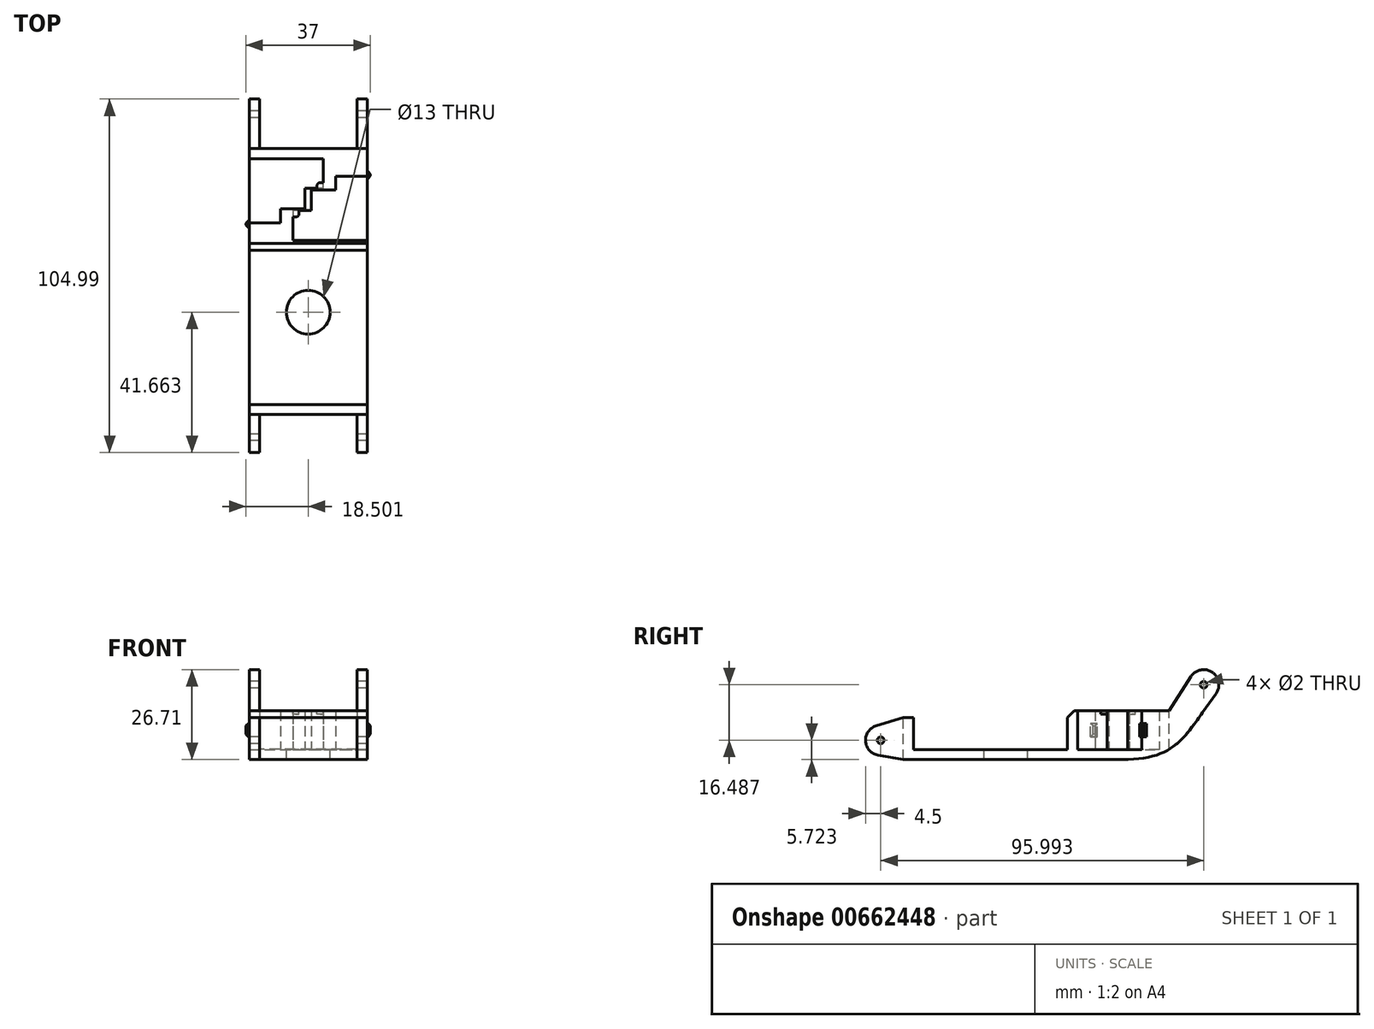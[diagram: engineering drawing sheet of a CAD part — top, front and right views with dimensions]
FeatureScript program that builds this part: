
annotation { "Feature Type Name" : "Feature", "Feature Type Description" : "" }
export const myFeature = defineFeature(function(context is Context, id is Id, definition is map)
    precondition{}
    {
        {
            var Q0;
            Q0=qCreatedBy(makeId("Top.planeOp"),FACE);
            var sketch = newSketch(context, id + "F0", { "sketchPlane" : qUnion([Q0])});
            skLineSegment(sketch, "E0.bottom", {"start": v(-9.64, 16.1) * mm, "end": v(7.86, 16.1) * mm});
            skLineSegment(sketch, "E0.top", {"start": v(-9.64, -29.7) * mm, "end": v(25.36, -29.7) * mm});
            skLineSegment(sketch, "E0.left", {"start": v(-9.64, 16.1) * mm, "end": v(-9.64, -29.7) * mm});
            skLineSegment(sketch, "E1", {"start": v(7.86, 16.1) * mm, "end": v(25.36, 16.1) * mm});
            skCircle(sketch, "E2", {"center": v(7.86, -2.29) * mm, "radius": 6.5 * mm});
            skLineSegment(sketch, "E3.MirrorCS", {"start": v(-9.64, 43.3) * mm, "end": v(-6.47, 43.3) * mm});
            skLineSegment(sketch, "E4.MirrorCS", {"start": v(7.86, 27.9) * mm, "end": v(7.86, 34.5) * mm});
            skLineSegment(sketch, "E5.MirrorCS", {"start": v(-9.64, 24.3) * mm, "end": v(-0.34, 24.3) * mm});
            skLineSegment(sketch, "E6.MirrorCS", {"start": v(12.36, 35.3) * mm, "end": v(12.36, 43.3) * mm});
            skLineSegment(sketch, "E7.MirrorCS", {"start": v(-6.47, 43.3) * mm, "end": v(12.36, 43.3) * mm});
            skLineSegment(sketch, "E8.MirrorCS", {"start": v(-9.64, 24.3) * mm, "end": v(-9.64, 43.3) * mm});
            skPoint(sketch, "E9", {"position": v(7.86, 31.6) * mm});
            skLineSegment(sketch, "E10", {"start": v(-9.64, 16.1) * mm, "end": v(-9.64, 19.1) * mm});
            skLineSegment(sketch, "E11", {"start": v(-9.64, 19.1) * mm, "end": v(25.36, 19.1) * mm});
            skLineSegment(sketch, "E12", {"start": v(-9.64, -29.7) * mm, "end": v(-9.64, -32.7) * mm});
            skLineSegment(sketch, "E13", {"start": v(-9.64, -32.7) * mm, "end": v(25.36, -32.7) * mm});
            skLineSegment(sketch, "E14", {"start": v(25.36, -32.7) * mm, "end": v(25.36, -29.7) * mm});
            skLineSegment(sketch, "E15", {"start": v(25.36, 19.1) * mm, "end": v(25.36, 19.1) * mm});
            skLineSegment(sketch, "E16", {"start": v(25.36, 19.1) * mm, "end": v(25.36, -29.7) * mm});
            skLineSegment(sketch, "E17.MirrorCS", {"start": v(25.36, 19.1) * mm, "end": v(22.2, 19.1) * mm});
            skLineSegment(sketch, "E18.MirrorCS", {"start": v(7.86, 34.5) * mm, "end": v(7.86, 27.9) * mm});
            skLineSegment(sketch, "E19.MirrorCS", {"start": v(25.36, 38.1) * mm, "end": v(16.06, 38.1) * mm});
            skLineSegment(sketch, "E20.MirrorCS", {"start": v(3.36, 27.1) * mm, "end": v(3.36, 19.1) * mm});
            skLineSegment(sketch, "E21.MirrorCS", {"start": v(22.2, 19.1) * mm, "end": v(3.36, 19.1) * mm});
            skLineSegment(sketch, "E22.MirrorCS", {"start": v(25.36, 38.1) * mm, "end": v(25.36, 19.1) * mm});
            skPoint(sketch, "E23", {"position": v(7.86, 30.8) * mm});
            skLineSegment(sketch, "E24", {"start": v(-9.64, 19.1) * mm, "end": v(-9.64, 24.3) * mm});
            skLineSegment(sketch, "E25", {"start": v(12.36, 43.3) * mm, "end": v(25.36, 43.3) * mm});
            skLineSegment(sketch, "E26", {"start": v(25.36, 43.3) * mm, "end": v(25.36, 38.1) * mm});
            skLineSegment(sketch, "E27", {"start": v(-9.64, 43.3) * mm, "end": v(-9.64, 46.3) * mm});
            skLineSegment(sketch, "E28", {"start": v(-9.64, 46.3) * mm, "end": v(25.36, 46.3) * mm});
            skLineSegment(sketch, "E29", {"start": v(25.36, 46.3) * mm, "end": v(25.36, 43.3) * mm});
            skLineSegment(sketch, "E30", {"start": v(25.36, -29.4) * mm, "end": v(-9.64, -29.4) * mm});
            skLineSegment(sketch, "E31", {"start": v(16.06, 38.1) * mm, "end": v(16.06, 34) * mm});
            skLineSegment(sketch, "E32", {"start": v(16.06, 34) * mm, "end": v(7.86, 34) * mm});
            skLineSegment(sketch, "E33", {"start": v(7.86, 34.5) * mm, "end": v(12.36, 34.5) * mm});
            skLineSegment(sketch, "E34", {"start": v(12.36, 34.5) * mm, "end": v(12.36, 35.3) * mm});
            skLineSegment(sketch, "E35", {"start": v(-0.34, 24.3) * mm, "end": v(-0.34, 28.4) * mm});
            skLineSegment(sketch, "E36", {"start": v(7.86, 27.9) * mm, "end": v(3.36, 27.9) * mm});
            skLineSegment(sketch, "E37", {"start": v(3.36, 27.9) * mm, "end": v(3.36, 27.1) * mm});
            skLineSegment(sketch, "E38", {"start": v(7.86, 34.5) * mm, "end": v(6.93, 34.5) * mm});
            skLineSegment(sketch, "E39", {"start": v(7.86, 27.9) * mm, "end": v(8.8, 27.9) * mm});
            skLineSegment(sketch, "E40", {"start": v(6.93, 34.5) * mm, "end": v(6.93, 28.4) * mm});
            skLineSegment(sketch, "E41", {"start": v(8.8, 27.9) * mm, "end": v(8.8, 34) * mm});
            skLineSegment(sketch, "E42", {"start": v(-0.34, 28.4) * mm, "end": v(7.86, 28.4) * mm});
            skSolve(sketch);
        }
        {
            var Q0;
            {var subQ2=sQuery(id+"F0.wireOp",EDGE,"E0.bottom");Q0=makeQuery(id+"F0.imprint","IMPRINT",FACE,{"disambiguationData":[TD([[makeQuery(id+"F0.imprint","IMPRINT",EDGE,{"derivedFrom":subQ2}),-1.0]])]});}
            var Q1;
            Q1=makeQuery(id+"F0.imprint","IMPRINT",FACE,{"disambiguationData":[TD([[makeQuery(id+"F0.imprint","IMPRINT",EDGE,{"derivedFrom":sQuery(id+"F0.wireOp",EDGE,"E0.top")}),-1.0]])]});
            var Q2;
            Q2=makeQuery(id+"F0.imprint","IMPRINT",FACE,{"disambiguationData":[TD([[makeQuery(id+"F0.imprint","IMPRINT",EDGE,{"derivedFrom":sQuery(id+"F0.wireOp",EDGE,"E0.bottom")}),1.0]])]});
            var Q3;
            {var subQ1=sQuery(id+"F0.wireOp",EDGE,"65957815-49e4-4ce0-b1aa-900a07c07509.MirrorCS");Q3=makeQuery(id+"F0.imprint","IMPRINT",FACE,{"disambiguationData":[TD([[makeQuery(id+"F0.imprint","IMPRINT",EDGE,{"derivedFrom":subQ1}),-1.0]])]});}
            var Q4;
            Q4=makeQuery(id+"F0.imprint","IMPRINT",FACE,{"disambiguationData":[TD([[makeQuery(id+"F0.imprint","IMPRINT",EDGE,{"derivedFrom":sQuery(id+"F0.wireOp",EDGE,"793e653a-9070-4513-9301-6aa9de76053a.MirrorCS")}),-1.0]])]});
            var Q5;
            {var subQ3=sQuery(id+"F0.wireOp",EDGE,"bcf4ff58-2fc9-42ac-b040-1ddef6c83d7c.MirrorCS");Q5=makeQuery(id+"F0.imprint","IMPRINT",FACE,{"disambiguationData":[TD([[makeQuery(id+"F0.imprint","IMPRINT",EDGE,{"derivedFrom":subQ3}),1.0]])]});}
            var Q6;
            Q6=makeQuery(id+"F0.imprint","IMPRINT",FACE,{"disambiguationData":[TD([[makeQuery(id+"F0.imprint","IMPRINT",EDGE,{"derivedFrom":sQuery(id+"F0.wireOp",EDGE,"793e653a-9070-4513-9301-6aa9de76053a.MirrorCS")}),1.0]])]});
            var Q7;
            Q7=makeQuery(id+"F0.imprint","IMPRINT",FACE,{"disambiguationData":[TD([[makeQuery(id+"F0.imprint","IMPRINT",EDGE,{"derivedFrom":sQuery(id+"F0.wireOp",EDGE,"E3.MirrorCS")}),1.0]])]});
            var Q8;
            {var subQ0=sQuery(id+"F0.wireOp",EDGE,"E0.top");Q8=makeQuery(id+"F0.imprint","IMPRINT",FACE,{"disambiguationData":[TD([[makeQuery(id+"F0.imprint","IMPRINT",EDGE,{"derivedFrom":subQ0}),1.0]])]});}
            var Q9;
            Q9=makeQuery(id+"F0.imprint","IMPRINT",FACE,{"disambiguationData":[TD([[makeQuery(id+"F0.imprint","IMPRINT",EDGE,{"derivedFrom":sQuery(id+"F0.wireOp",EDGE,"E6.MirrorCS")}),-1.0]])]});
            var Q10;
            Q10=makeQuery(id+"F0.imprint","IMPRINT",FACE,{"disambiguationData":[TD([[makeQuery(id+"F0.imprint","IMPRINT",EDGE,{"derivedFrom":sQuery(id+"F0.wireOp",EDGE,"E5.MirrorCS")}),-1.0]])]});
            var Q11;
            {var subQ3=sQuery(id+"F0.wireOp",EDGE,"E38");Q11=makeQuery(id+"F0.imprint","IMPRINT",FACE,{"disambiguationData":[TD([[makeQuery(id+"F0.imprint","IMPRINT",EDGE,{"derivedFrom":subQ3}),1.0]])]});}
            var Q12;
            {var subQ0=sQuery(id+"F0.wireOp",EDGE,"E39");Q12=makeQuery(id+"F0.imprint","IMPRINT",FACE,{"disambiguationData":[TD([[makeQuery(id+"F0.imprint","IMPRINT",EDGE,{"derivedFrom":subQ0}),1.0]])]});}
            var Q13;
            Q13=makeQuery(id+"F0.imprint","IMPRINT",FACE,{"disambiguationData":[TD([[makeQuery(id+"F0.imprint","IMPRINT",EDGE,{"derivedFrom":sQuery(id+"F0.wireOp",EDGE,"E3.MirrorCS")}),-1.0]])]});
            var Q14;
            Q14=makeQuery(id+"F0.imprint","IMPRINT",FACE,{"disambiguationData":[TD([[makeQuery(id+"F0.imprint","IMPRINT",EDGE,{"derivedFrom":sQuery(id+"F0.wireOp",EDGE,"E19.MirrorCS")}),1.0]])]});
            extrude(context, id + "F1", {"entities" : qUnion([Q0, Q1, Q2, Q3, Q4, Q5, Q6, Q7, Q8, Q9, Q10, Q11, Q12, Q13, Q14]), "oppositeDirection" : true, "depth" : 3 * mm, "offsetDistance" : 25 * mm});
        }
        {
            var Q0;
            Q0=makeQuery(id+"F0.imprint","IMPRINT",FACE,{"disambiguationData":[TD([[makeQuery(id+"F0.imprint","IMPRINT",EDGE,{"derivedFrom":sQuery(id+"F0.wireOp",EDGE,"E0.top")}),-1.0]])]});
            var Q1;
            Q1=makeQuery(id+"F0.imprint","IMPRINT",FACE,{"disambiguationData":[TD([[makeQuery(id+"F0.imprint","IMPRINT",EDGE,{"derivedFrom":sQuery(id+"F0.wireOp",EDGE,"E0.bottom")}),1.0]])]});
            extrude(context, id + "F2", {"entities" : qUnion([Q0, Q1]), "operationType" : NewBodyOperationType.ADD, "depth" : 9.5 * mm, "offsetDistance" : 25 * mm});
        }
        {
            var Q0;
            {var subQ1=sQuery(id+"F0.wireOp",EDGE,"65957815-49e4-4ce0-b1aa-900a07c07509.MirrorCS");Q0=makeQuery(id+"F0.imprint","IMPRINT",FACE,{"disambiguationData":[TD([[makeQuery(id+"F0.imprint","IMPRINT",EDGE,{"derivedFrom":subQ1}),-1.0]])]});}
            var Q1;
            Q1=makeQuery(id+"F0.imprint","IMPRINT",FACE,{"disambiguationData":[TD([[makeQuery(id+"F0.imprint","IMPRINT",EDGE,{"derivedFrom":sQuery(id+"F0.wireOp",EDGE,"793e653a-9070-4513-9301-6aa9de76053a.MirrorCS")}),-1.0]])]});
            var Q2;
            Q2=makeQuery(id+"F0.imprint","IMPRINT",FACE,{"disambiguationData":[TD([[makeQuery(id+"F0.imprint","IMPRINT",EDGE,{"derivedFrom":sQuery(id+"F0.wireOp",EDGE,"E3.MirrorCS")}),1.0]])]});
            var Q3;
            Q3=makeQuery(id+"F0.imprint","IMPRINT",FACE,{"disambiguationData":[TD([[makeQuery(id+"F0.imprint","IMPRINT",EDGE,{"derivedFrom":sQuery(id+"F0.wireOp",EDGE,"E5.MirrorCS")}),-1.0]])]});
            var Q4;
            {var subQ0=sQuery(id+"F0.wireOp",EDGE,"E39");Q4=makeQuery(id+"F0.imprint","IMPRINT",FACE,{"disambiguationData":[TD([[makeQuery(id+"F0.imprint","IMPRINT",EDGE,{"derivedFrom":subQ0}),1.0]])]});}
            var Q5;
            {var subQ3=sQuery(id+"F0.wireOp",EDGE,"E38");Q5=makeQuery(id+"F0.imprint","IMPRINT",FACE,{"disambiguationData":[TD([[makeQuery(id+"F0.imprint","IMPRINT",EDGE,{"derivedFrom":subQ3}),1.0]])]});}
            var Q6;
            Q6=makeQuery(id+"F0.imprint","IMPRINT",FACE,{"disambiguationData":[TD([[makeQuery(id+"F0.imprint","IMPRINT",EDGE,{"derivedFrom":sQuery(id+"F0.wireOp",EDGE,"E6.MirrorCS")}),-1.0]])]});
            var Q7;
            Q7=makeQuery(id+"F0.imprint","IMPRINT",FACE,{"disambiguationData":[TD([[makeQuery(id+"F0.imprint","IMPRINT",EDGE,{"derivedFrom":sQuery(id+"F0.wireOp",EDGE,"E0.bottom")}),1.0]])]});
            extrude(context, id + "F3", {"entities" : qUnion([Q0, Q1, Q2, Q3, Q4, Q5, Q6, Q7]), "operationType" : NewBodyOperationType.ADD, "depth" : 11.5 * mm, "offsetDistance" : 25 * mm});
        }
        {
            var Q0;
            {var subQ0=sQuery(id+"F0.wireOp",EDGE,"E29");var subQ1=sQuery(id+"F0.wireOp",EDGE,"E26");var subQ2=sQuery(id+"F0.wireOp",EDGE,"E16");var subQ3=sQuery(id+"F0.wireOp",EDGE,"E14");Q0=makeQuery(id+"F3.boolean.opBoolean","MERGE",FACE,{"derivedFrom":[makeQuery(id+"F2.boolean.opBoolean","MERGE",FACE,{"derivedFrom":[makeQuery(id+"F1.opExtrude","SWEPT_FACE",FACE,{"disambiguationData":[OSD([subQ3,subQ2,sQuery(id+"F0.wireOp",EDGE,"E22.MirrorCS"),subQ1,subQ0])]}),makeQuery(id+"F2.opExtrude","SWEPT_FACE",FACE,{"disambiguationData":[OSD([subQ3])]}),makeQuery(id+"F2.opExtrude","SWEPT_FACE",FACE,{"disambiguationData":[OSD([subQ2])]})]}),makeQuery(id+"F3.opExtrude","SWEPT_FACE",FACE,{"disambiguationData":[OSD([subQ2])]}),makeQuery(id+"F3.opExtrude","SWEPT_FACE",FACE,{"disambiguationData":[OSD([subQ1,subQ0])]})]});}
            var sketch = newSketch(context, id + "F4", { "sketchPlane" : qUnion([Q0])});
            skLineSegment(sketch, "E43.6", {"start": v(46.3, -3) * mm, "end": v(46.3, 11.5) * mm});
            skLineSegment(sketch, "E43.7", {"start": v(46.3, 11.5) * mm, "end": v(38.1, 11.5) * mm});
            skLineSegment(sketch, "E43.8", {"start": v(-32.7, -3) * mm, "end": v(-32.7, 9.5) * mm});
            skCircle(sketch, "E44", {"center": v(56.54, 19.2) * mm, "radius": 4.5 * mm});
            skLineSegment(sketch, "E45", {"start": v(46.3, -3) * mm, "end": v(60.21, 16.6) * mm});
            skLineSegment(sketch, "E46", {"start": v(46.3, 11.5) * mm, "end": v(52.75, 21.63) * mm});
            skCircle(sketch, "E47", {"center": v(-39.45, 2.72) * mm, "radius": 4.5 * mm});
            skLineSegment(sketch, "E48", {"start": v(-32.7, 9.5) * mm, "end": v(-40.77, 7.03) * mm});
            skLineSegment(sketch, "E49", {"start": v(-32.7, -3) * mm, "end": v(-40.21, -1.71) * mm});
            skSolve(sketch);
        }
        {
            var Q0;
            {var subQ0=sQuery(id+"F4.wireOp",EDGE,"E47");var subQ1=makeQuery(id+"F4.imprint","INTERSECT",VERTEX,{"derivedFrom":[subQ0,sQuery(id+"F4.wireOp",EDGE,"PAik2qhj-YHKu-fe6H-CUS2-yW6YpYjkYPtX")]});Q0=makeQuery(id+"F4.imprint","IMPRINT",FACE,{"disambiguationData":[TD([[makeQuery(id+"F4.imprint","IMPRINT",EDGE,{"disambiguationData":[TD([[subQ1,1.0]])],"derivedFrom":subQ0}),1.0]])]});}
            var Q1;
            Q1=makeQuery(id+"F4.imprint","IMPRINT",FACE,{"disambiguationData":[TD([[makeQuery(id+"F4.imprint","IMPRINT",EDGE,{"derivedFrom":sQuery(id+"F4.wireOp",EDGE,"E43.8")}),1.0]])]});
            var Q2;
            Q2=makeQuery(id+"F4.imprint","IMPRINT",FACE,{"disambiguationData":[TD([[makeQuery(id+"F4.imprint","IMPRINT",EDGE,{"derivedFrom":sQuery(id+"F4.wireOp",EDGE,"E43.6")}),-1.0]])]});
            var Q3;
            {var subQ0=sQuery(id+"F4.wireOp",EDGE,"E44");var subQ1=makeQuery(id+"F4.imprint","INTERSECT",VERTEX,{"derivedFrom":[subQ0,sQuery(id+"F4.wireOp",EDGE,"E45")]});Q3=makeQuery(id+"F4.imprint","IMPRINT",FACE,{"disambiguationData":[TD([[makeQuery(id+"F4.imprint","IMPRINT",EDGE,{"disambiguationData":[TD([[subQ1,1.0]])],"derivedFrom":subQ0}),1.0]])]});}
            extrude(context, id + "F5", {"entities" : qUnion([Q0, Q1, Q2, Q3]), "operationType" : NewBodyOperationType.ADD, "oppositeDirection" : true, "depth" : 3 * mm, "offsetDistance" : 25 * mm});
        }
        {
            var Q0;
            {var subQ0=sQuery(id+"F0.wireOp",EDGE,"E27");var subQ1=sQuery(id+"F0.wireOp",EDGE,"E24");var subQ2=sQuery(id+"F0.wireOp",EDGE,"E10");var subQ3=sQuery(id+"F0.wireOp",EDGE,"E12");Q0=makeQuery(id+"F3.boolean.opBoolean","MERGE",FACE,{"derivedFrom":[makeQuery(id+"F2.boolean.opBoolean","MERGE",FACE,{"derivedFrom":[makeQuery(id+"F1.opExtrude","SWEPT_FACE",FACE,{"disambiguationData":[OSD([sQuery(id+"F0.wireOp",EDGE,"E0.left"),sQuery(id+"F0.wireOp",EDGE,"E8.MirrorCS"),subQ2,subQ3,subQ1,subQ0])]}),makeQuery(id+"F2.opExtrude","SWEPT_FACE",FACE,{"disambiguationData":[OSD([subQ2])]}),makeQuery(id+"F2.opExtrude","SWEPT_FACE",FACE,{"disambiguationData":[OSD([subQ3])]})]}),makeQuery(id+"F3.opExtrude","SWEPT_FACE",FACE,{"disambiguationData":[OSD([subQ2,subQ1])]}),makeQuery(id+"F3.opExtrude","SWEPT_FACE",FACE,{"disambiguationData":[OSD([subQ0])]})]});}
            var sketch = newSketch(context, id + "F6", { "sketchPlane" : qUnion([Q0])});
            skLineSegment(sketch, "E50.0", {"start": v(-46.3, -3) * mm, "end": v(-60.21, 16.6) * mm});
            skArc(sketch, "E50.1", {"start": v(-60.21, 16.6) * mm, "mid": v(-59.06, 22.94) * mm, "end": v(-52.75, 21.63) * mm});
            skLineSegment(sketch, "E50.2", {"start": v(-46.3, 11.5) * mm, "end": v(-52.75, 21.63) * mm});
            skLineSegment(sketch, "E50.3", {"start": v(-46.3, -3) * mm, "end": v(-46.3, 11.5) * mm});
            skLineSegment(sketch, "E50.4", {"start": v(32.7, -3) * mm, "end": v(32.7, 9.5) * mm});
            skLineSegment(sketch, "E50.5", {"start": v(32.7, 9.5) * mm, "end": v(40.77, 7.03) * mm});
            skArc(sketch, "E50.6", {"start": v(40.77, 7.03) * mm, "mid": v(43.94, 2.44) * mm, "end": v(40.21, -1.71) * mm});
            skLineSegment(sketch, "E50.7", {"start": v(32.7, -3) * mm, "end": v(40.21, -1.71) * mm});
            skSolve(sketch);
        }
        {
            var Q0;
            Q0=makeQuery(id+"F6.imprint","IMPRINT",FACE,{"disambiguationData":[TD([[makeQuery(id+"F6.imprint","IMPRINT",EDGE,{"derivedFrom":sQuery(id+"F6.wireOp",EDGE,"E50.0")}),-1.0]])]});
            var Q1;
            Q1=makeQuery(id+"F6.imprint","IMPRINT",FACE,{"disambiguationData":[TD([[makeQuery(id+"F6.imprint","IMPRINT",EDGE,{"derivedFrom":sQuery(id+"F6.wireOp",EDGE,"E50.4")}),-1.0]])]});
            extrude(context, id + "F7", {"entities" : qUnion([Q0, Q1]), "operationType" : NewBodyOperationType.ADD, "oppositeDirection" : true, "depth" : 3 * mm, "offsetDistance" : 25 * mm});
        }
        {
            var Q0;
            {var subQ0=sQuery(id+"F0.wireOp",EDGE,"E27");var subQ1=sQuery(id+"F0.wireOp",EDGE,"E24");var subQ2=sQuery(id+"F0.wireOp",EDGE,"E10");var subQ3=sQuery(id+"F0.wireOp",EDGE,"E12");Q0=makeQuery(id+"F7.boolean.opBoolean","MERGE",FACE,{"derivedFrom":[makeQuery(id+"F3.boolean.opBoolean","MERGE",FACE,{"derivedFrom":[makeQuery(id+"F2.boolean.opBoolean","MERGE",FACE,{"derivedFrom":[makeQuery(id+"F1.opExtrude","SWEPT_FACE",FACE,{"disambiguationData":[OSD([sQuery(id+"F0.wireOp",EDGE,"E0.left"),sQuery(id+"F0.wireOp",EDGE,"E8.MirrorCS"),subQ2,subQ3,subQ1,subQ0])]}),makeQuery(id+"F2.opExtrude","SWEPT_FACE",FACE,{"disambiguationData":[OSD([subQ2])]}),makeQuery(id+"F2.opExtrude","SWEPT_FACE",FACE,{"disambiguationData":[OSD([subQ3])]})]}),makeQuery(id+"F3.opExtrude","SWEPT_FACE",FACE,{"disambiguationData":[OSD([subQ2,subQ1])]}),makeQuery(id+"F3.opExtrude","SWEPT_FACE",FACE,{"disambiguationData":[OSD([subQ0])]})]}),makeQuery(id+"F7.opExtrude","CAP_FACE",FACE,{"disambiguationData":[OSD([sQuery(id+"F6.wireOp",EDGE,"E50.0"),sQuery(id+"F6.wireOp",EDGE,"E50.1"),sQuery(id+"F6.wireOp",EDGE,"E50.2"),sQuery(id+"F6.wireOp",EDGE,"E50.3")])],"isStart":true}),makeQuery(id+"F7.opExtrude","CAP_FACE",FACE,{"disambiguationData":[OSD([sQuery(id+"F6.wireOp",EDGE,"E50.4"),sQuery(id+"F6.wireOp",EDGE,"E50.5"),sQuery(id+"F6.wireOp",EDGE,"E50.6"),sQuery(id+"F6.wireOp",EDGE,"E50.7")])],"isStart":true})]});}
            var sketch = newSketch(context, id + "F8", { "sketchPlane" : qUnion([Q0])});
            skArc(sketch, "E51.0", {"start": v(-60.21, 16.6) * mm, "mid": v(-59.06, 22.94) * mm, "end": v(-52.75, 21.63) * mm});
            skArc(sketch, "E51.1", {"start": v(40.77, 7.03) * mm, "mid": v(43.94, 2.44) * mm, "end": v(40.21, -1.71) * mm});
            skCircle(sketch, "E52", {"center": v(-56.54, 19.2) * mm, "radius": 1 * mm});
            skCircle(sketch, "E53", {"center": v(39.45, 2.72) * mm, "radius": 1 * mm});
            skSolve(sketch);
        }
        {
            var Q0;
            Q0=makeQuery(id+"F8.imprint","IMPRINT",FACE,{"disambiguationData":[TD([[makeQuery(id+"F8.imprint","IMPRINT",EDGE,{"derivedFrom":sQuery(id+"F8.wireOp",EDGE,"E52")}),1.0]])]});
            var Q1;
            Q1=makeQuery(id+"F8.imprint","IMPRINT",FACE,{"disambiguationData":[TD([[makeQuery(id+"F8.imprint","IMPRINT",EDGE,{"derivedFrom":sQuery(id+"F8.wireOp",EDGE,"E53")}),1.0]])]});
            extrude(context, id + "F9", {"entities" : qUnion([Q0, Q1]), "operationType" : NewBodyOperationType.REMOVE, "endBound" : BoundingType.THROUGH_ALL, "oppositeDirection" : true, "depth" : 25 * mm, "offsetDistance" : 25 * mm});
        }
        {
            var Q0;
            {var subQ0=sQuery(id+"F0.wireOp",EDGE,"E29");var subQ1=sQuery(id+"F0.wireOp",EDGE,"E26");var subQ2=sQuery(id+"F0.wireOp",EDGE,"E16");var subQ3=sQuery(id+"F0.wireOp",EDGE,"E14");Q0=makeQuery(id+"F5.boolean.opBoolean","MERGE",FACE,{"derivedFrom":[makeQuery(id+"F3.boolean.opBoolean","MERGE",FACE,{"derivedFrom":[makeQuery(id+"F2.boolean.opBoolean","MERGE",FACE,{"derivedFrom":[makeQuery(id+"F1.opExtrude","SWEPT_FACE",FACE,{"disambiguationData":[OSD([subQ3,subQ2,sQuery(id+"F0.wireOp",EDGE,"E22.MirrorCS"),subQ1,subQ0])]}),makeQuery(id+"F2.opExtrude","SWEPT_FACE",FACE,{"disambiguationData":[OSD([subQ3])]}),makeQuery(id+"F2.opExtrude","SWEPT_FACE",FACE,{"disambiguationData":[OSD([subQ2])]})]}),makeQuery(id+"F3.opExtrude","SWEPT_FACE",FACE,{"disambiguationData":[OSD([subQ2])]}),makeQuery(id+"F3.opExtrude","SWEPT_FACE",FACE,{"disambiguationData":[OSD([subQ1,subQ0])]})]}),makeQuery(id+"F5.opExtrude","CAP_FACE",FACE,{"disambiguationData":[OSD([sQuery(id+"F4.wireOp",EDGE,"E43.6"),sQuery(id+"F4.wireOp",EDGE,"E44"),sQuery(id+"F4.wireOp",EDGE,"E45"),sQuery(id+"F4.wireOp",EDGE,"E46")])],"isStart":true}),makeQuery(id+"F5.opExtrude","CAP_FACE",FACE,{"disambiguationData":[OSD([sQuery(id+"F4.wireOp",EDGE,"E43.8"),sQuery(id+"F4.wireOp",EDGE,"E47"),sQuery(id+"F4.wireOp",EDGE,"E48"),sQuery(id+"F4.wireOp",EDGE,"E49")])],"isStart":true})]});}
            var sketch = newSketch(context, id + "F10", { "sketchPlane" : qUnion([Q0])});
            skLineSegment(sketch, "E54.0", {"start": v(38.1, 11.5) * mm, "end": v(38.1, 0) * mm});
            skPoint(sketch, "E55", {"position": v(38.1, 5.75) * mm});
            skLineSegment(sketch, "E56", {"start": v(35.03, 5.75) * mm, "end": v(42.1, 5.75) * mm, "construction": true});
            skLineSegment(sketch, "E57", {"start": v(37.5, 5.75) * mm, "end": v(37.5, 7.75) * mm});
            skLineSegment(sketch, "E58", {"start": v(37.5, 7.75) * mm, "end": v(39.5, 7.75) * mm});
            skLineSegment(sketch, "E59", {"start": v(39.5, 7.75) * mm, "end": v(39.5, 5.75) * mm});
            skLineSegment(sketch, "E60.MirrorCS", {"start": v(37.5, 3.75) * mm, "end": v(39.5, 3.75) * mm});
            skLineSegment(sketch, "E61.MirrorCS", {"start": v(37.5, 5.75) * mm, "end": v(37.5, 3.75) * mm});
            skLineSegment(sketch, "E62.MirrorCS", {"start": v(39.5, 3.75) * mm, "end": v(39.5, 5.75) * mm});
            skSolve(sketch);
        }
        {
            var Q0;
            {var subQ4=sQuery(id+"F10.wireOp",EDGE,"E59");Q0=makeQuery(id+"F10.imprint","IMPRINT",FACE,{"disambiguationData":[TD([[makeQuery(id+"F10.imprint","IMPRINT",EDGE,{"derivedFrom":subQ4}),-1.0]])]});}
            var Q1;
            {var subQ5=sQuery(id+"F10.wireOp",EDGE,"E57");Q1=makeQuery(id+"F10.imprint","IMPRINT",FACE,{"disambiguationData":[TD([[makeQuery(id+"F10.imprint","IMPRINT",EDGE,{"derivedFrom":subQ5}),-1.0]])]});}
            extrude(context, id + "F11", {"entities" : qUnion([Q0, Q1]), "operationType" : NewBodyOperationType.ADD, "depth" : 1 * mm, "offsetDistance" : 25 * mm});
        }
        {
            var Q0;
            {var subQ0=sQuery(id+"F0.wireOp",EDGE,"E27");var subQ1=sQuery(id+"F0.wireOp",EDGE,"E24");var subQ2=sQuery(id+"F0.wireOp",EDGE,"E10");var subQ3=sQuery(id+"F0.wireOp",EDGE,"E12");Q0=makeQuery(id+"F7.boolean.opBoolean","MERGE",FACE,{"derivedFrom":[makeQuery(id+"F3.boolean.opBoolean","MERGE",FACE,{"derivedFrom":[makeQuery(id+"F2.boolean.opBoolean","MERGE",FACE,{"derivedFrom":[makeQuery(id+"F1.opExtrude","SWEPT_FACE",FACE,{"disambiguationData":[OSD([sQuery(id+"F0.wireOp",EDGE,"E0.left"),sQuery(id+"F0.wireOp",EDGE,"E8.MirrorCS"),subQ2,subQ3,subQ1,subQ0])]}),makeQuery(id+"F2.opExtrude","SWEPT_FACE",FACE,{"disambiguationData":[OSD([subQ2])]}),makeQuery(id+"F2.opExtrude","SWEPT_FACE",FACE,{"disambiguationData":[OSD([subQ3])]})]}),makeQuery(id+"F3.opExtrude","SWEPT_FACE",FACE,{"disambiguationData":[OSD([subQ2,subQ1])]}),makeQuery(id+"F3.opExtrude","SWEPT_FACE",FACE,{"disambiguationData":[OSD([subQ0])]})]}),makeQuery(id+"F7.opExtrude","CAP_FACE",FACE,{"disambiguationData":[OSD([sQuery(id+"F6.wireOp",EDGE,"E50.0"),sQuery(id+"F6.wireOp",EDGE,"E50.1"),sQuery(id+"F6.wireOp",EDGE,"E50.2"),sQuery(id+"F6.wireOp",EDGE,"E50.3")])],"isStart":true}),makeQuery(id+"F7.opExtrude","CAP_FACE",FACE,{"disambiguationData":[OSD([sQuery(id+"F6.wireOp",EDGE,"E50.4"),sQuery(id+"F6.wireOp",EDGE,"E50.5"),sQuery(id+"F6.wireOp",EDGE,"E50.6"),sQuery(id+"F6.wireOp",EDGE,"E50.7")])],"isStart":true})]});}
            var sketch = newSketch(context, id + "F12", { "sketchPlane" : qUnion([Q0])});
            skLineSegment(sketch, "E63", {"start": v(-24.3, 5.75) * mm, "end": v(-30.81, 5.75) * mm, "construction": true});
            skLineSegment(sketch, "E64", {"start": v(-24.9, 5.75) * mm, "end": v(-24.9, 7.75) * mm});
            skLineSegment(sketch, "E65", {"start": v(-24.9, 7.75) * mm, "end": v(-22.9, 7.75) * mm});
            skLineSegment(sketch, "E66", {"start": v(-22.9, 7.75) * mm, "end": v(-22.9, 5.75) * mm});
            skLineSegment(sketch, "E67.MirrorCS", {"start": v(-24.9, 5.75) * mm, "end": v(-24.9, 3.75) * mm});
            skLineSegment(sketch, "E68.MirrorCS", {"start": v(-22.9, 3.75) * mm, "end": v(-22.9, 5.75) * mm});
            skLineSegment(sketch, "E69.MirrorCS", {"start": v(-24.9, 3.75) * mm, "end": v(-22.9, 3.75) * mm});
            skSolve(sketch);
        }
        {
            var Q0;
            {var subQ1=sQuery(id+"F12.wireOp",EDGE,"E66");Q0=makeQuery(id+"F12.imprint","IMPRINT",FACE,{"disambiguationData":[TD([[makeQuery(id+"F12.imprint","IMPRINT",EDGE,{"derivedFrom":subQ1}),-1.0]])]});}
            var Q1;
            {var subQ5=sQuery(id+"F12.wireOp",EDGE,"E64");Q1=makeQuery(id+"F12.imprint","IMPRINT",FACE,{"disambiguationData":[TD([[makeQuery(id+"F12.imprint","IMPRINT",EDGE,{"derivedFrom":subQ5}),-1.0]])]});}
            extrude(context, id + "F13", {"entities" : qUnion([Q0, Q1]), "operationType" : NewBodyOperationType.ADD, "depth" : 1 * mm, "offsetDistance" : 25 * mm});
        }
        {
            var Q0;
            Q0=makeQuery(id+"F13.opExtrude","CAP_EDGE",EDGE,{"disambiguationData":[OSD([sQuery(id+"F12.wireOp",EDGE,"E64"),sQuery(id+"F12.wireOp",EDGE,"E67.MirrorCS")])],"isStart":false});
            var Q1;
            Q1=makeQuery(id+"F13.opExtrude","CAP_EDGE",EDGE,{"disambiguationData":[OSD([sQuery(id+"F12.wireOp",EDGE,"E66"),sQuery(id+"F12.wireOp",EDGE,"E68.MirrorCS")])],"isStart":false});
            var Q2;
            Q2=makeQuery(id+"F13.opExtrude","CAP_EDGE",EDGE,{"disambiguationData":[OSD([sQuery(id+"F12.wireOp",EDGE,"E65")])],"isStart":false});
            var Q3;
            Q3=makeQuery(id+"F13.opExtrude","CAP_EDGE",EDGE,{"disambiguationData":[OSD([sQuery(id+"F12.wireOp",EDGE,"E69.MirrorCS")])],"isStart":false});
            var Q4;
            Q4=makeQuery(id+"F11.opExtrude","CAP_EDGE",EDGE,{"disambiguationData":[OSD([sQuery(id+"F10.wireOp",EDGE,"E58")])],"isStart":false});
            var Q5;
            Q5=makeQuery(id+"F11.opExtrude","CAP_EDGE",EDGE,{"disambiguationData":[OSD([sQuery(id+"F10.wireOp",EDGE,"E57"),sQuery(id+"F10.wireOp",EDGE,"E61.MirrorCS")])],"isStart":false});
            var Q6;
            Q6=makeQuery(id+"F11.opExtrude","CAP_EDGE",EDGE,{"disambiguationData":[OSD([sQuery(id+"F10.wireOp",EDGE,"E60.MirrorCS")])],"isStart":false});
            var Q7;
            Q7=makeQuery(id+"F11.opExtrude","CAP_EDGE",EDGE,{"disambiguationData":[OSD([sQuery(id+"F10.wireOp",EDGE,"E59"),sQuery(id+"F10.wireOp",EDGE,"E62.MirrorCS")])],"isStart":false});
            chamfer(context, id + "F14", {"entities" : qUnion([Q0, Q1, Q2, Q3, Q4, Q5, Q6, Q7]), "width" : .75 * mm, "tangentPropagation" : true});
        }
        {
            var Q0;
            Q0=makeQuery(id+"F3.opExtrude","CAP_FACE",FACE,{"disambiguationData":[OSD([sQuery(id+"F0.wireOp",EDGE,"E0.bottom"),sQuery(id+"F0.wireOp",EDGE,"E1"),sQuery(id+"F0.wireOp",EDGE,"E3.MirrorCS"),sQuery(id+"F0.wireOp",EDGE,"E5.MirrorCS"),sQuery(id+"F0.wireOp",EDGE,"E6.MirrorCS"),sQuery(id+"F0.wireOp",EDGE,"E7.MirrorCS"),sQuery(id+"F0.wireOp",EDGE,"E10"),sQuery(id+"F0.wireOp",EDGE,"E11"),sQuery(id+"F0.wireOp",EDGE,"E16"),sQuery(id+"F0.wireOp",EDGE,"E19.MirrorCS"),sQuery(id+"F0.wireOp",EDGE,"E20.MirrorCS"),sQuery(id+"F0.wireOp",EDGE,"E24"),sQuery(id+"F0.wireOp",EDGE,"E26"),sQuery(id+"F0.wireOp",EDGE,"E27"),sQuery(id+"F0.wireOp",EDGE,"E28"),sQuery(id+"F0.wireOp",EDGE,"E29"),sQuery(id+"F0.wireOp",EDGE,"E31"),sQuery(id+"F0.wireOp",EDGE,"E32"),sQuery(id+"F0.wireOp",EDGE,"E33"),sQuery(id+"F0.wireOp",EDGE,"E34"),sQuery(id+"F0.wireOp",EDGE,"E35"),sQuery(id+"F0.wireOp",EDGE,"E36"),sQuery(id+"F0.wireOp",EDGE,"E37"),sQuery(id+"F0.wireOp",EDGE,"E38"),sQuery(id+"F0.wireOp",EDGE,"E39"),sQuery(id+"F0.wireOp",EDGE,"E40"),sQuery(id+"F0.wireOp",EDGE,"E41"),sQuery(id+"F0.wireOp",EDGE,"E42")])],"isStart":false});
            var sketch = newSketch(context, id + "F15", { "sketchPlane" : qUnion([Q0])});
            skLineSegment(sketch, "E70.0", {"start": v(12.36, 34.5) * mm, "end": v(6.93, 34.5) * mm});
            skLineSegment(sketch, "E70.1", {"start": v(8.8, 27.9) * mm, "end": v(3.36, 27.9) * mm});
            skLineSegment(sketch, "E71", {"start": v(5.12, 27.9) * mm, "end": v(5.12, 25.96) * mm});
            skPoint(sketch, "E71.endSnap0", {"position": v(3.36, 25.96) * mm});
            skLineSegment(sketch, "E72", {"start": v(5.12, 25.96) * mm, "end": v(3.36, 25.96) * mm});
            skLineSegment(sketch, "E73", {"start": v(3.36, 27.9) * mm, "end": v(3.36, 25.96) * mm});
            skLineSegment(sketch, "E74", {"start": v(10.48, 34.5) * mm, "end": v(10.48, 36.23) * mm});
            skPoint(sketch, "E74.endSnap0", {"position": v(12.36, 36.23) * mm});
            skLineSegment(sketch, "E75", {"start": v(10.48, 36.23) * mm, "end": v(12.36, 36.23) * mm});
            skSolve(sketch);
        }
        {
            var Q0;
            {var subQ3=sQuery(id+"F15.wireOp",EDGE,"E74");Q0=makeQuery(id+"F15.imprint","IMPRINT",FACE,{"disambiguationData":[TD([[makeQuery(id+"F15.imprint","IMPRINT",EDGE,{"derivedFrom":subQ3}),-1.0]])]});}
            var Q1;
            {var subQ2=sQuery(id+"F15.wireOp",EDGE,"E71");Q1=makeQuery(id+"F15.imprint","IMPRINT",FACE,{"disambiguationData":[TD([[makeQuery(id+"F15.imprint","IMPRINT",EDGE,{"derivedFrom":subQ2}),-1.0]])]});}
            extrude(context, id + "F16", {"entities" : qUnion([Q0, Q1]), "operationType" : NewBodyOperationType.ADD, "oppositeDirection" : true, "depth" : 1 * mm, "offsetDistance" : 25 * mm});
        }
        {
            var Q0;
            {var subQ0=sQuery(id+"F0.wireOp",EDGE,"E27");var subQ1=sQuery(id+"F0.wireOp",EDGE,"E24");var subQ2=sQuery(id+"F0.wireOp",EDGE,"E10");var subQ3=sQuery(id+"F0.wireOp",EDGE,"E12");Q0=makeQuery(id+"F7.boolean.opBoolean","MERGE",FACE,{"derivedFrom":[makeQuery(id+"F3.boolean.opBoolean","MERGE",FACE,{"derivedFrom":[makeQuery(id+"F2.boolean.opBoolean","MERGE",FACE,{"derivedFrom":[makeQuery(id+"F1.opExtrude","SWEPT_FACE",FACE,{"disambiguationData":[OSD([sQuery(id+"F0.wireOp",EDGE,"E0.left"),sQuery(id+"F0.wireOp",EDGE,"E8.MirrorCS"),subQ2,subQ3,subQ1,subQ0])]}),makeQuery(id+"F2.opExtrude","SWEPT_FACE",FACE,{"disambiguationData":[OSD([subQ2])]}),makeQuery(id+"F2.opExtrude","SWEPT_FACE",FACE,{"disambiguationData":[OSD([subQ3])]})]}),makeQuery(id+"F3.opExtrude","SWEPT_FACE",FACE,{"disambiguationData":[OSD([subQ2,subQ1])]}),makeQuery(id+"F3.opExtrude","SWEPT_FACE",FACE,{"disambiguationData":[OSD([subQ0])]})]}),makeQuery(id+"F7.opExtrude","CAP_FACE",FACE,{"disambiguationData":[OSD([sQuery(id+"F6.wireOp",EDGE,"E50.0"),sQuery(id+"F6.wireOp",EDGE,"E50.1"),sQuery(id+"F6.wireOp",EDGE,"E50.2"),sQuery(id+"F6.wireOp",EDGE,"E50.3")])],"isStart":true}),makeQuery(id+"F7.opExtrude","CAP_FACE",FACE,{"disambiguationData":[OSD([sQuery(id+"F6.wireOp",EDGE,"E50.4"),sQuery(id+"F6.wireOp",EDGE,"E50.5"),sQuery(id+"F6.wireOp",EDGE,"E50.6"),sQuery(id+"F6.wireOp",EDGE,"E50.7")])],"isStart":true})]});}
            var sketch = newSketch(context, id + "F17", { "sketchPlane" : qUnion([Q0])});
            skLineSegment(sketch, "E76.0", {"start": v(-46.3, -3) * mm, "end": v(-60.21, 16.6) * mm});
            skLineSegment(sketch, "E76.1", {"start": v(-46.3, -3) * mm, "end": v(32.7, -3) * mm});
            skFitSpline(sketch, "E77", {"points": [v(-56.2, 10.95) * mm, v(-32.24, -3) * mm], "startDerivative": vector(19.25, -27.12) * mm, "endDerivative": vector(42.2, 0) * mm});
            skSolve(sketch);
        }
        {
            var Q0;
            {var subQ3=sQuery(id+"F17.wireOp",EDGE,"E77");Q0=makeQuery(id+"F17.imprint","IMPRINT",FACE,{"disambiguationData":[TD([[makeQuery(id+"F17.imprint","IMPRINT",EDGE,{"derivedFrom":subQ3}),-1.0]])]});}
            extrude(context, id + "F18", {"entities" : qUnion([Q0]), "operationType" : NewBodyOperationType.REMOVE, "endBound" : BoundingType.THROUGH_ALL, "oppositeDirection" : true, "depth" : 25 * mm, "offsetDistance" : 25 * mm});
        }
        {
            var Q0;
            Q0=makeQuery(id+"F16.opExtrude","SWEPT_EDGE",EDGE,{"disambiguationData":[OSD([sQuery(id+"F15.wireOp",EDGE,"E71"),sQuery(id+"F15.wireOp",EDGE,"E72")])]});
            var Q1;
            Q1=makeQuery(id+"F16.opExtrude","SWEPT_EDGE",EDGE,{"disambiguationData":[OSD([sQuery(id+"F15.wireOp",EDGE,"E74"),sQuery(id+"F15.wireOp",EDGE,"E75")])]});
            fillet(context, id + "F19", {"entities" : qUnion([Q0, Q1]), "radius" : 1 * mm, "tangentPropagation" : true, "allowEdgeOverflow" : false});
        }
        {
            var Q0;
            Q0=makeQuery(id+"F3.opExtrude","CAP_EDGE",EDGE,{"disambiguationData":[OSD([sQuery(id+"F0.wireOp",EDGE,"E0.bottom"),sQuery(id+"F0.wireOp",EDGE,"E1")])],"isStart":false});
            chamfer(context, id + "F20", {"entities" : qUnion([Q0]), "chamferType" : ChamferType.TWO_OFFSETS, "width1" : 2 * mm, "oppositeDirection" : false, "width2" : 2 * mm, "tangentPropagation" : true});
        }
    });
